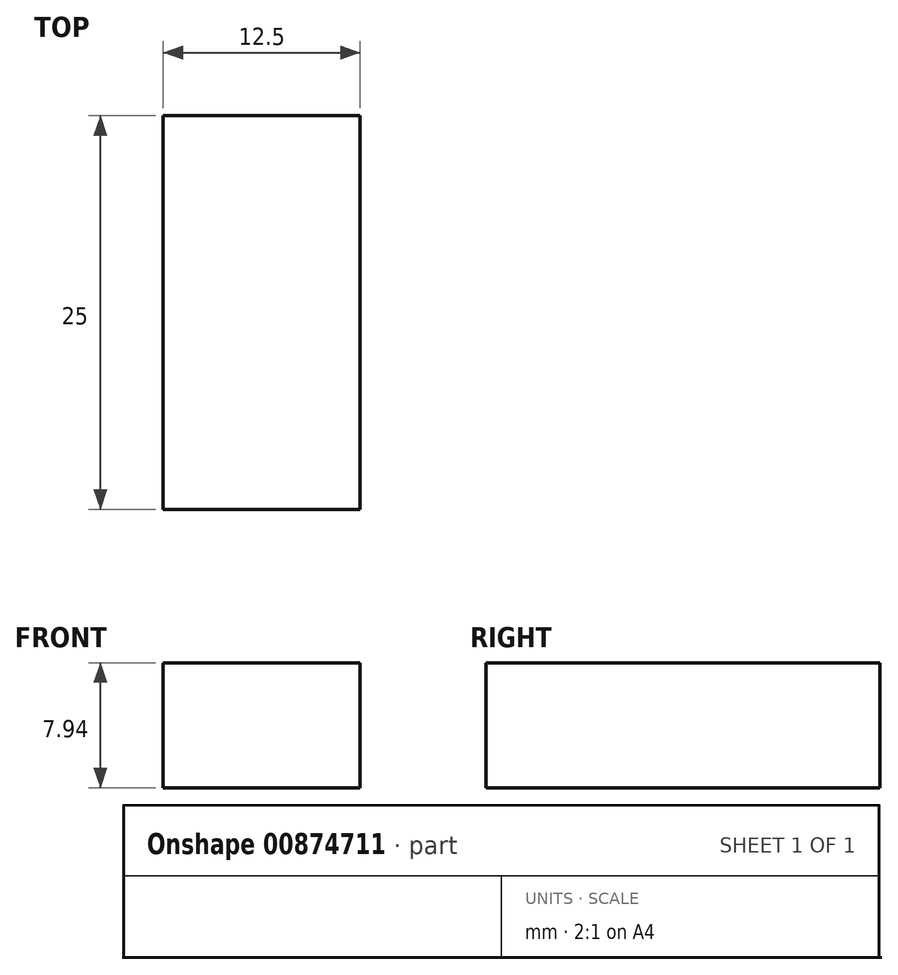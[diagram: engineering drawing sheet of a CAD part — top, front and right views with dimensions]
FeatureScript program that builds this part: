
annotation { "Feature Type Name" : "Feature", "Feature Type Description" : "" }
export const myFeature = defineFeature(function(context is Context, id is Id, definition is map)
    precondition{}
    {
        {
            var Q0;
            Q0=qCreatedBy(makeId("Top.planeOp"),FACE);
            var sketch = newSketch(context, id + "F0", { "sketchPlane" : qUnion([Q0])});
            skLineSegment(sketch, "E0.bottom", {"start": v(0, 0) * mm, "end": v(12.5, 0) * mm});
            skLineSegment(sketch, "E0.top", {"start": v(0, 25) * mm, "end": v(12.5, 25) * mm});
            skLineSegment(sketch, "E0.left", {"start": v(0, 0) * mm, "end": v(0, 25) * mm});
            skLineSegment(sketch, "E0.right", {"start": v(12.5, 0) * mm, "end": v(12.5, 25) * mm});
            skSolve(sketch);
        }
        {
            var Q0;
            Q0=makeQuery(id+"F0.imprint","IMPRINT",FACE,{"disambiguationData":[TD([[makeQuery(id+"F0.imprint","IMPRINT",EDGE,{"derivedFrom":sQuery(id+"F0.wireOp",EDGE,"E0.bottom")}),1.0]])]});
            extrude(context, id + "F1", {"entities" : qUnion([Q0]), "depth" : 7.94 * mm, "offsetDistance" : 25.4 * mm});
        }
    });
